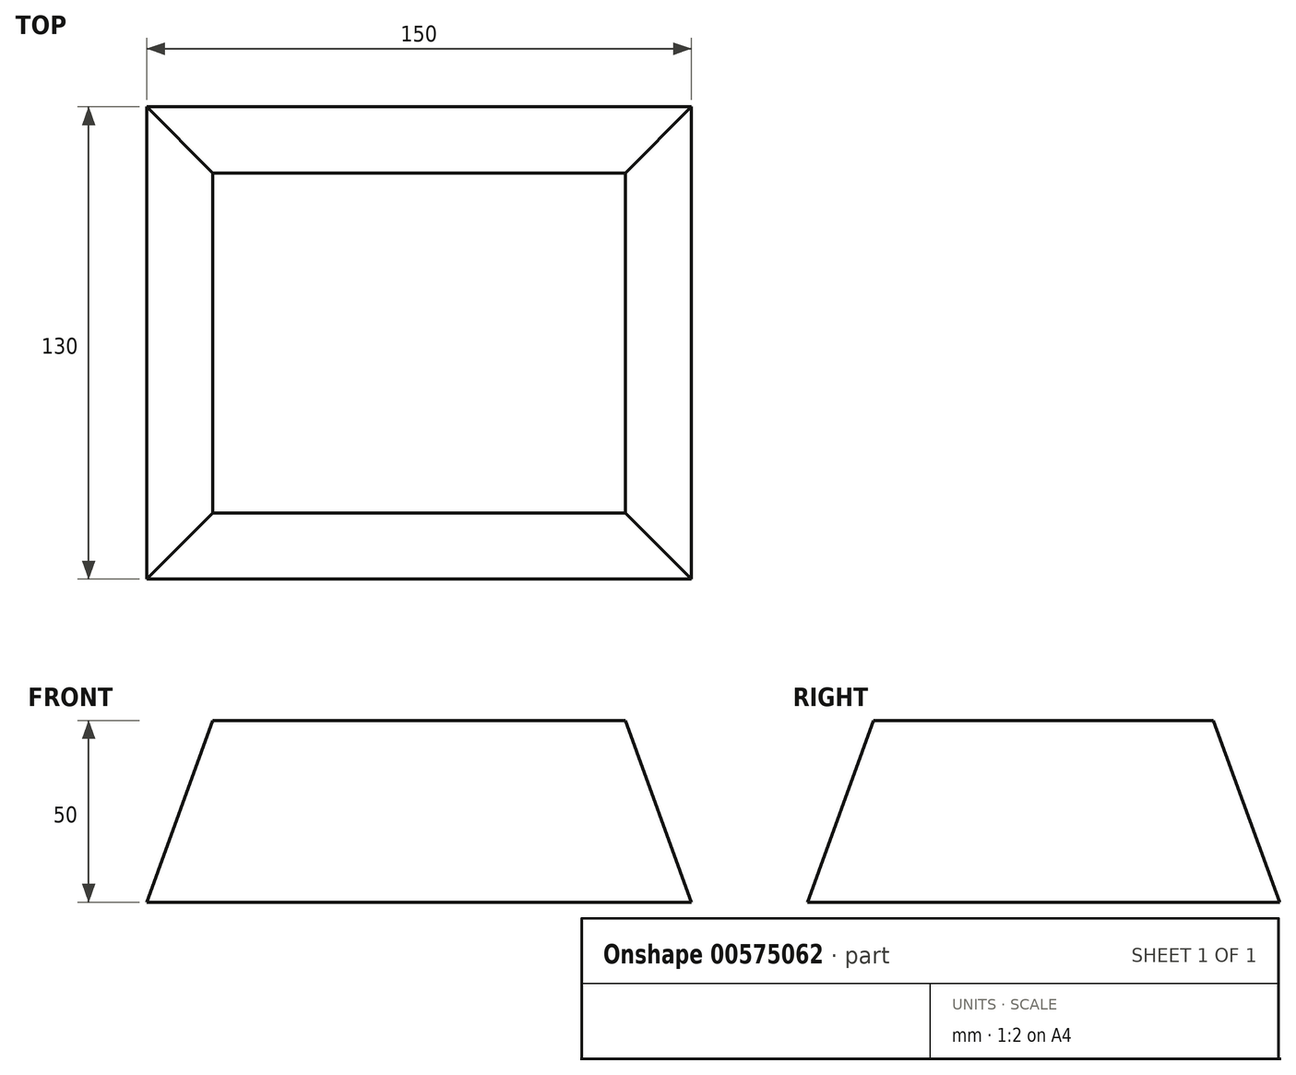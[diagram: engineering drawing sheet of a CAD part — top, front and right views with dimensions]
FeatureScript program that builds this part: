
annotation { "Feature Type Name" : "Feature", "Feature Type Description" : "" }
export const myFeature = defineFeature(function(context is Context, id is Id, definition is map)
    precondition{}
    {
        {
            var Q0;
            Q0=qCreatedBy(makeId("Top.planeOp"),FACE);
            var sketch = newSketch(context, id + "F0", { "sketchPlane" : qUnion([Q0])});
            skLineSegment(sketch, "E0.bottom", {"start": v(75, 65) * mm, "end": v(-75, 65) * mm});
            skLineSegment(sketch, "E0.top", {"start": v(75, -65) * mm, "end": v(-75, -65) * mm});
            skLineSegment(sketch, "E0.left", {"start": v(75, 65) * mm, "end": v(75, -65) * mm});
            skLineSegment(sketch, "E0.right", {"start": v(-75, 65) * mm, "end": v(-75, -65) * mm});
            skPoint(sketch, "E0.middle", {"position": v(0, 0) * mm});
            skSolve(sketch);
        }
        {
            var Q0;
            Q0=makeQuery(id+"F0.imprint","IMPRINT",FACE,{"disambiguationData":[TD([[makeQuery(id+"F0.imprint","IMPRINT",EDGE,{"derivedFrom":sQuery(id+"F0.wireOp",EDGE,"E0.bottom")}),1.0]])]});
            extrude(context, id + "F1", {"entities" : qUnion([Q0]), "depth" : 50 * mm, "offsetDistance" : 25 * mm, "hasDraft" : true, "draftAngle" : 20 * degree, "draftPullDirection" : true});
        }
    });
